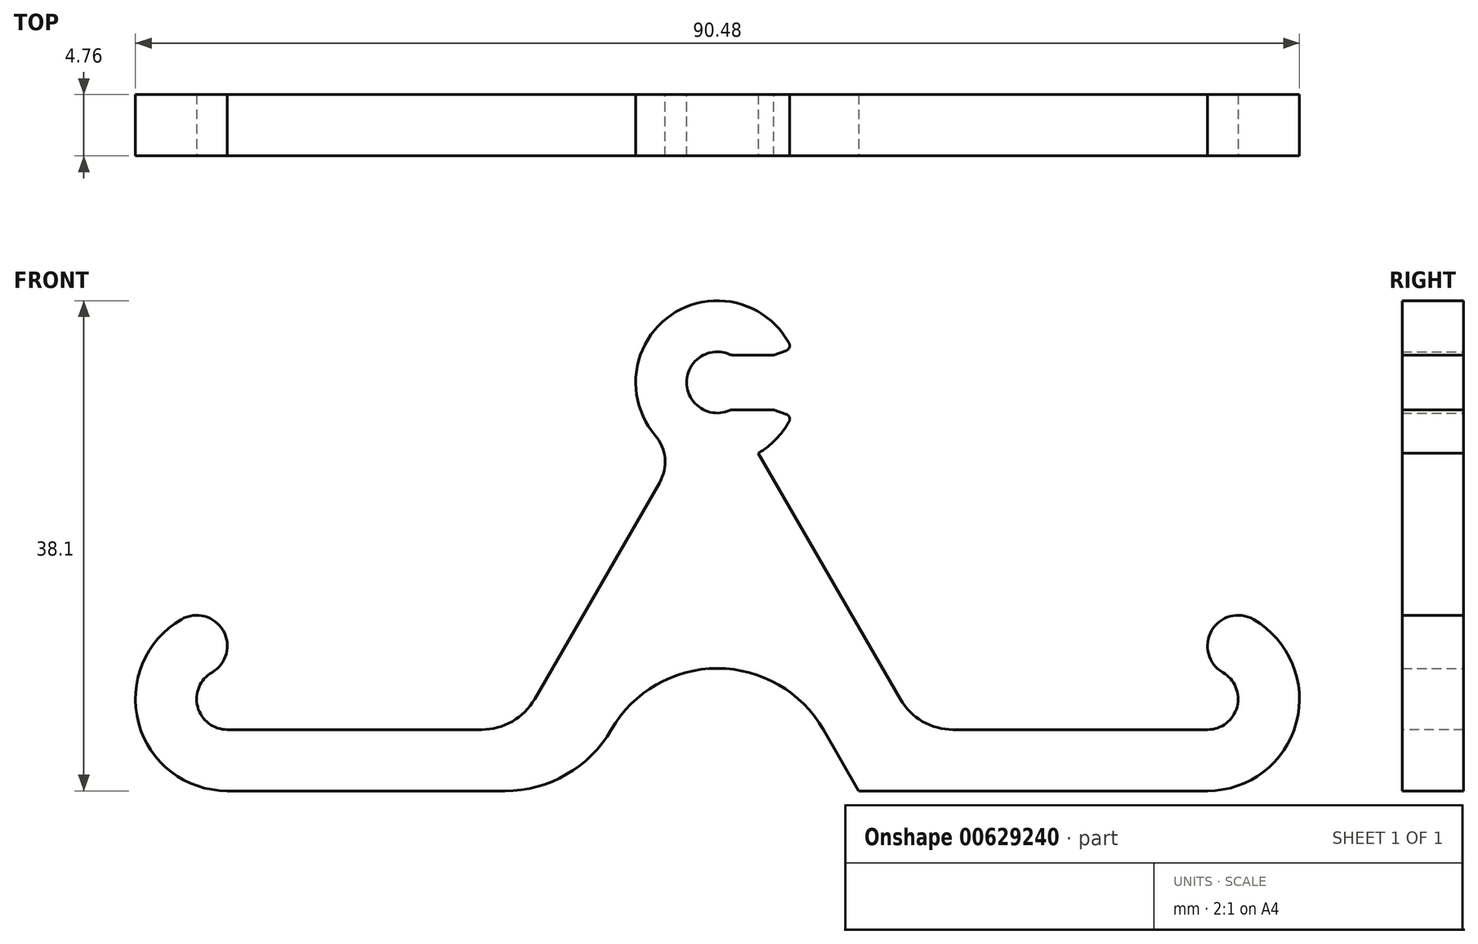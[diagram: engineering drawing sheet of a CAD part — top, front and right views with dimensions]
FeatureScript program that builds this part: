
annotation { "Feature Type Name" : "Feature", "Feature Type Description" : "" }
export const myFeature = defineFeature(function(context is Context, id is Id, definition is map)
    precondition{}
    {
        {
            var Q0;
            Q0=qCreatedBy(makeId("Front.planeOp"),FACE);
            var sketch = newSketch(context, id + "F0", { "sketchPlane" : qUnion([Q0])});
            skLineSegment(sketch, "E0", {"start": v(-38.1, 0) * mm, "end": v(38.1, 0) * mm});
            skLineSegment(sketch, "E1", {"start": v(0, 0) * mm, "end": v(0, 31.75) * mm, "construction": true});
            skArc(sketch, "E2", {"start": v(-38.1, 14.29) * mm, "mid": v(-45.24, 7.14) * mm, "end": v(-38.1, 0) * mm});
            skArc(sketch, "E3", {"start": v(38.1, 0) * mm, "mid": v(45.24, 7.14) * mm, "end": v(38.1, 14.29) * mm});
            skArc(sketch, "E4", {"start": v(1.07, 33.88) * mm, "mid": v(-2.38, 31.75) * mm, "end": v(1.07, 29.62) * mm});
            skArc(sketch, "E5", {"start": v(5.98, 33.88) * mm, "mid": v(-6.35, 31.75) * mm, "end": v(5.98, 29.62) * mm});
            skLineSegment(sketch, "E6", {"start": v(-38.1, 4.76) * mm, "end": v(-18.33, 4.76) * mm});
            skArc(sketch, "E7", {"start": v(-38.1, 9.53) * mm, "mid": v(-40.48, 7.14) * mm, "end": v(-38.1, 4.76) * mm});
            skArc(sketch, "E8", {"start": v(38.1, 4.76) * mm, "mid": v(40.48, 7.14) * mm, "end": v(38.1, 9.53) * mm});
            skLineSegment(sketch, "E9", {"start": v(38.1, 14.29) * mm, "end": v(38.1, 9.53) * mm});
            skLineSegment(sketch, "E10", {"start": v(-38.1, 14.29) * mm, "end": v(-38.1, 9.53) * mm});
            skArc(sketch, "E11", {"start": v(-18.33, 4.76) * mm, "mid": v(-15.95, 5.4) * mm, "end": v(-14.2, 7.14) * mm});
            skArc(sketch, "E12", {"start": v(14.2, 7.14) * mm, "mid": v(15.95, 5.4) * mm, "end": v(18.33, 4.76) * mm});
            skLineSegment(sketch, "E13", {"start": v(-14.2, 7.14) * mm, "end": v(-3.18, 26.25) * mm});
            skLineSegment(sketch, "E14.trimOffspring", {"start": v(18.33, 4.76) * mm, "end": v(38.1, 4.76) * mm});
            skLineSegment(sketch, "E15", {"start": v(14.2, 7.14) * mm, "end": v(3.18, 26.25) * mm});
            skLineSegment(sketch, "E16", {"start": v(1.07, 33.88) * mm, "end": v(5.98, 33.88) * mm});
            skLineSegment(sketch, "E17", {"start": v(1.07, 29.62) * mm, "end": v(5.98, 29.62) * mm});
            skLineSegment(sketch, "E18", {"start": v(0, 31.75) * mm, "end": v(6.35, 31.75) * mm, "construction": true});
            skSolve(sketch);
        }
        {
            var Q0;
            Q0=makeQuery(id+"F0.imprint","IMPRINT",FACE,{"disambiguationData":[TD([[makeQuery(id+"F0.imprint","IMPRINT",EDGE,{"derivedFrom":sQuery(id+"F0.wireOp",EDGE,"E0")}),1.0]])]});
            extrude(context, id + "F1", {"entities" : qUnion([Q0]), "endBound" : BoundingType.SYMMETRIC, "oppositeDirection" : true, "depth" : 4.76 * mm, "offsetDistance" : 25.4 * mm});
        }
        {
            var Q0;
            Q0=makeQuery(id+"F0.imprint","IMPRINT",FACE,{"disambiguationData":[TD([[makeQuery(id+"F0.imprint","IMPRINT",EDGE,{"derivedFrom":sQuery(id+"F0.wireOp",EDGE,"E4")}),-1.0]])]});
            extrude(context, id + "F2", {"entities" : qUnion([Q0]), "operationType" : NewBodyOperationType.ADD, "endBound" : BoundingType.SYMMETRIC, "depth" : 4.76 * mm, "offsetDistance" : 25.4 * mm});
        }
        {
            var Q0;
            Q0=makeQuery(id+"F2.opExtrude","SWEPT_EDGE",EDGE,{"disambiguationData":[OSD([sQuery(id+"F0.wireOp",EDGE,"E5"),sQuery(id+"F0.wireOp",EDGE,"E16")])]});
            chamfer(context, id + "F3", {"entities" : qUnion([Q0]), "chamferType" : ChamferType.TWO_OFFSETS, "width1" : 0.4 * mm, "oppositeDirection" : false, "width2" : 1.59 * mm, "tangentPropagation" : true});
        }
        {
            var Q0;
            Q0=makeQuery(id+"F2.opExtrude","SWEPT_EDGE",EDGE,{"disambiguationData":[OSD([sQuery(id+"F0.wireOp",EDGE,"E5"),sQuery(id+"F0.wireOp",EDGE,"E17")])]});
            chamfer(context, id + "F4", {"entities" : qUnion([Q0]), "chamferType" : ChamferType.TWO_OFFSETS, "width1" : 1.59 * mm, "oppositeDirection" : false, "width2" : 0.4 * mm, "tangentPropagation" : true});
        }
        {
            var Q0;
            {var subQ0=sQuery(id+"F0.wireOp",EDGE,"E13");var subQ10=sQuery(id+"F0.wireOp",EDGE,"E5");var subQ15=sQuery(id+"F0.wireOp",EDGE,"E16");Q0=makeQuery(id+"F3.opChamfer","BLEND_EDGE",EDGE,{"blendedFrom":[makeQuery(id+"F2.opExtrude","SWEPT_EDGE",EDGE,{"disambiguationData":[OSD([subQ10,subQ15])]}),makeQuery(id+"F2.boolean.opBoolean","SPLIT",FACE,{"disambiguationData":[TD([makeQuery(id+"F1.opExtrude","SWEPT_FACE",FACE,{"disambiguationData":[OSD([subQ0])]})])],"derivedFrom":makeQuery(id+"F2.opExtrude","SWEPT_FACE",FACE,{"disambiguationData":[OSD([subQ10])]})})],"blendedInto":[makeQuery(id+"F2.boolean.opBoolean","SPLIT",FACE,{"disambiguationData":[TD([makeQuery(id+"F1.opExtrude","SWEPT_FACE",FACE,{"disambiguationData":[OSD([subQ0])]})])],"derivedFrom":makeQuery(id+"F2.opExtrude","SWEPT_FACE",FACE,{"disambiguationData":[OSD([subQ10])]})})]});}
            var Q1;
            {var subQ0=sQuery(id+"F0.wireOp",EDGE,"E15");var subQ1=sQuery(id+"F0.wireOp",EDGE,"E17");var subQ3=sQuery(id+"F0.wireOp",EDGE,"E5");Q1=makeQuery(id+"F4.opChamfer","BLEND_EDGE",EDGE,{"blendedFrom":[makeQuery(id+"F2.opExtrude","SWEPT_EDGE",EDGE,{"disambiguationData":[OSD([subQ3,subQ1])]}),makeQuery(id+"F2.boolean.opBoolean","SPLIT",FACE,{"disambiguationData":[TD([makeQuery(id+"F1.opExtrude","SWEPT_FACE",FACE,{"disambiguationData":[OSD([subQ0])]})])],"derivedFrom":makeQuery(id+"F2.opExtrude","SWEPT_FACE",FACE,{"disambiguationData":[OSD([subQ3])]})})],"blendedInto":[makeQuery(id+"F2.boolean.opBoolean","SPLIT",FACE,{"disambiguationData":[TD([makeQuery(id+"F1.opExtrude","SWEPT_FACE",FACE,{"disambiguationData":[OSD([subQ0])]})])],"derivedFrom":makeQuery(id+"F2.opExtrude","SWEPT_FACE",FACE,{"disambiguationData":[OSD([subQ3])]})})]});}
            var Q2;
            Q2=makeQuery(id+"F2.opExtrude","SWEPT_EDGE",EDGE,{"disambiguationData":[OSD([sQuery(id+"F0.wireOp",EDGE,"E4"),sQuery(id+"F0.wireOp",EDGE,"E17")])]});
            var Q3;
            Q3=makeQuery(id+"F2.opExtrude","SWEPT_EDGE",EDGE,{"disambiguationData":[OSD([sQuery(id+"F0.wireOp",EDGE,"E4"),sQuery(id+"F0.wireOp",EDGE,"E16")])]});
            fillet(context, id + "F5", {"entities" : qUnion([Q0, Q1, Q2, Q3]), "radius" : 0.4 * mm, "tangentPropagation" : true, "allowEdgeOverflow" : false});
        }
        {
            var Q0;
            Q0=makeQuery(id+"F1.opExtrude","SWEPT_EDGE",EDGE,{"disambiguationData":[OSD([sQuery(id+"F0.wireOp",EDGE,"E5"),sQuery(id+"F0.wireOp",EDGE,"E15")])]});
            var Q1;
            Q1=makeQuery(id+"F1.opExtrude","SWEPT_EDGE",EDGE,{"disambiguationData":[OSD([sQuery(id+"F0.wireOp",EDGE,"E5"),sQuery(id+"F0.wireOp",EDGE,"E13")])]});
            fillet(context, id + "F6", {"entities" : qUnion([Q0, Q1]), "radius" : 3.17 * mm, "tangentPropagation" : true, "allowEdgeOverflow" : false});
        }
        {
            var Q0;
            Q0=makeQuery(id+"F1.opExtrude","SWEPT_EDGE",EDGE,{"disambiguationData":[OSD([sQuery(id+"F0.wireOp",EDGE,"E3"),sQuery(id+"F0.wireOp",EDGE,"E9")])]});
            var Q1;
            Q1=makeQuery(id+"F1.opExtrude","SWEPT_EDGE",EDGE,{"disambiguationData":[OSD([sQuery(id+"F0.wireOp",EDGE,"E8"),sQuery(id+"F0.wireOp",EDGE,"E9")])]});
            var Q2;
            Q2=makeQuery(id+"F1.opExtrude","SWEPT_EDGE",EDGE,{"disambiguationData":[OSD([sQuery(id+"F0.wireOp",EDGE,"E2"),sQuery(id+"F0.wireOp",EDGE,"E10")])]});
            var Q3;
            Q3=makeQuery(id+"F1.opExtrude","SWEPT_EDGE",EDGE,{"disambiguationData":[OSD([sQuery(id+"F0.wireOp",EDGE,"E7"),sQuery(id+"F0.wireOp",EDGE,"E10")])]});
            fillet(context, id + "F7", {"entities" : qUnion([Q0, Q1, Q2, Q3]), "radius" : 2.38 * mm, "tangentPropagation" : true, "allowEdgeOverflow" : false});
        }
        {
            var Q0;
            {var subQ0=sQuery(id+"F0.wireOp",EDGE,"E5");Q0=makeQuery(id+"F2.boolean.opBoolean","MERGE",FACE,{"derivedFrom":[makeQuery(id+"F1.opExtrude","CAP_FACE",FACE,{"disambiguationData":[OSD([sQuery(id+"F0.wireOp",EDGE,"E0"),sQuery(id+"F0.wireOp",EDGE,"E2"),sQuery(id+"F0.wireOp",EDGE,"E3"),subQ0,sQuery(id+"F0.wireOp",EDGE,"E6"),sQuery(id+"F0.wireOp",EDGE,"E7"),sQuery(id+"F0.wireOp",EDGE,"E8"),sQuery(id+"F0.wireOp",EDGE,"E9"),sQuery(id+"F0.wireOp",EDGE,"E10"),sQuery(id+"F0.wireOp",EDGE,"E11"),sQuery(id+"F0.wireOp",EDGE,"E12"),sQuery(id+"F0.wireOp",EDGE,"E13"),sQuery(id+"F0.wireOp",EDGE,"E14.trimOffspring"),sQuery(id+"F0.wireOp",EDGE,"E15")])],"isStart":true}),makeQuery(id+"F2.opExtrude","CAP_FACE",FACE,{"disambiguationData":[OSD([sQuery(id+"F0.wireOp",EDGE,"E4"),subQ0,sQuery(id+"F0.wireOp",EDGE,"E16"),sQuery(id+"F0.wireOp",EDGE,"E17")])],"isStart":false})]});}
            var sketch = newSketch(context, id + "F8", { "sketchPlane" : qUnion([Q0])});
            skLineSegment(sketch, "E19", {"start": v(0, 19.05) * mm, "end": v(-11, 0) * mm});
            skLineSegment(sketch, "E20", {"start": v(11, 0) * mm, "end": v(0, 19.05) * mm});
            skLineSegment(sketch, "E21", {"start": v(0, 0) * mm, "end": v(0, 19.05) * mm, "construction": true});
            skLineSegment(sketch, "E22.0", {"start": v(-38.1, 0) * mm, "end": v(38.1, 0) * mm});
            skSolve(sketch);
        }
        {
            var Q0;
            Q0=makeQuery(id+"F8.imprint","IMPRINT",FACE,{"disambiguationData":[TD([[makeQuery(id+"F8.imprint","IMPRINT",EDGE,{"derivedFrom":sQuery(id+"F8.wireOp",EDGE,"E19")}),1.0]])]});
            extrude(context, id + "F9", {"entities" : qUnion([Q0]), "operationType" : NewBodyOperationType.REMOVE, "endBound" : BoundingType.THROUGH_ALL, "oppositeDirection" : true, "depth" : 25.4 * mm, "offsetDistance" : 25.4 * mm});
        }
        {
            var Q0;
            Q0=makeQuery(id+"F9.boolean.opBoolean","COPY",EDGE,{"derivedFrom":makeQuery(id+"F9.opExtrude","SWEPT_EDGE",EDGE,{"disambiguationData":[OSD([sQuery(id+"F8.wireOp",EDGE,"E19"),sQuery(id+"F8.wireOp",EDGE,"E20")])]})});
            var Q1;
            Q1=makeQuery(id+"F9.boolean.opBoolean","COPY",EDGE,{"derivedFrom":makeQuery(id+"F9.opExtrude","SWEPT_EDGE",EDGE,{"disambiguationData":[OSD([sQuery(id+"F8.wireOp",EDGE,"WrWGPINC-GbhH-olMk-xjGW-4O7OX8yPscfC"),sQuery(id+"F8.wireOp",EDGE,"E20")])]})});
            var Q2;
            Q2=makeQuery(id+"F9.boolean.opBoolean","COPY",EDGE,{"derivedFrom":makeQuery(id+"F9.opExtrude","SWEPT_EDGE",EDGE,{"disambiguationData":[OSD([sQuery(id+"F8.wireOp",EDGE,"E19"),sQuery(id+"F8.wireOp",EDGE,"WrWGPINC-GbhH-olMk-xjGW-4O7OX8yPscfC")])]})});
            fillet(context, id + "F10", {"entities" : qUnion([Q0, Q1, Q2]), "radius" : 9.52 * mm, "tangentPropagation" : true, "allowEdgeOverflow" : false});
        }
    });
